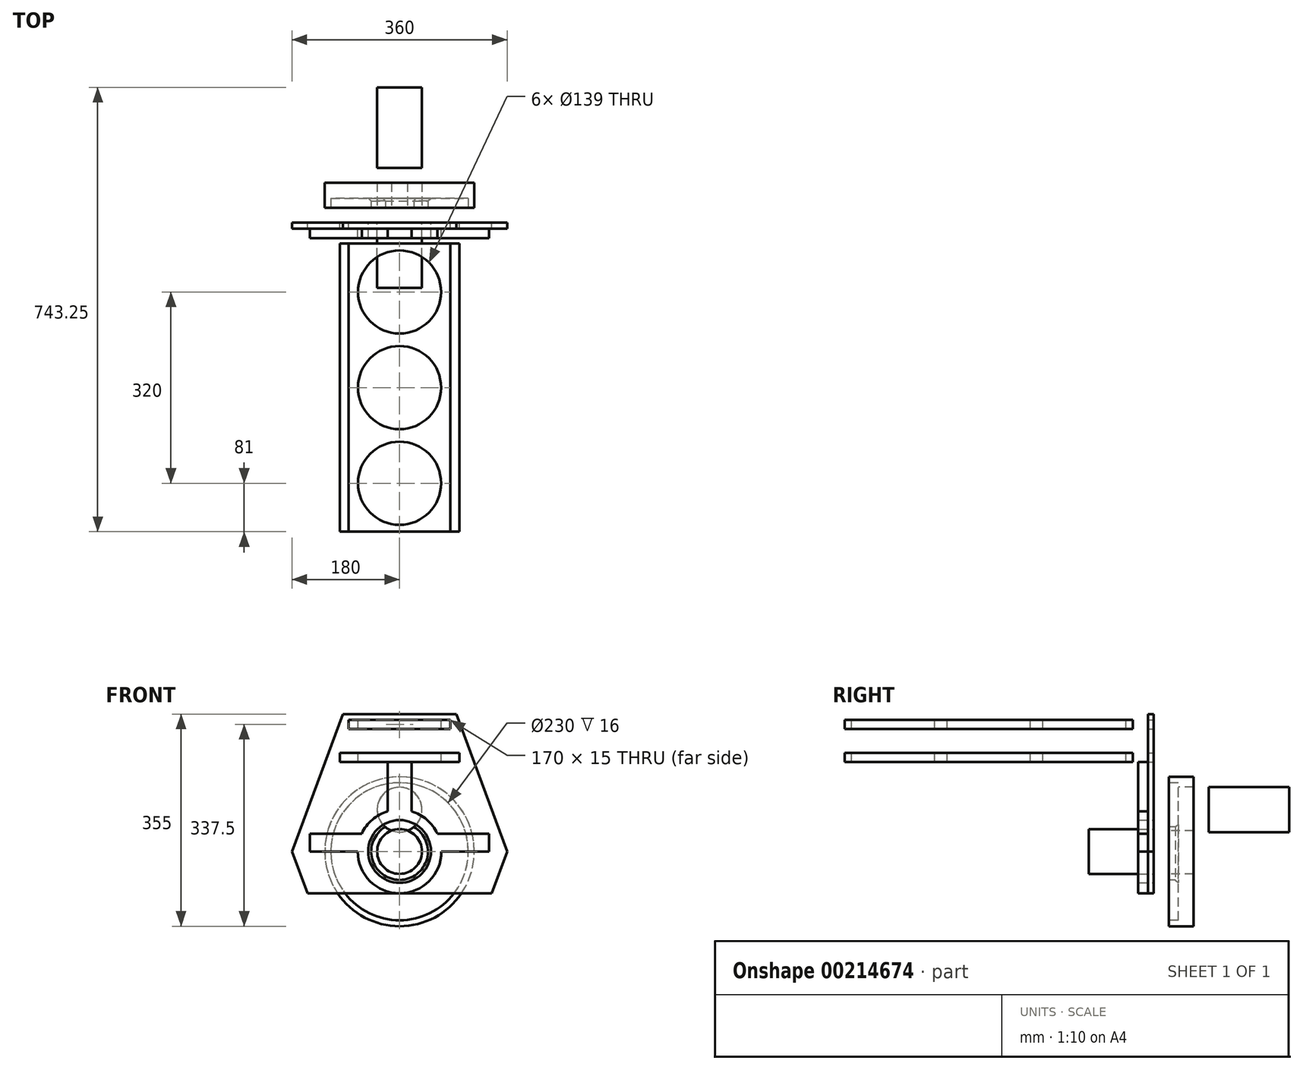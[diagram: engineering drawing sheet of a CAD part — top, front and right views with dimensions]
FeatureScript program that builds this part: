
annotation { "Feature Type Name" : "Feature", "Feature Type Description" : "" }
export const myFeature = defineFeature(function(context is Context, id is Id, definition is map)
    precondition{}
    {
        {
            var Q0;
            Q0=qCreatedBy(makeId("Front.planeOp"),FACE);
            var sketch = newSketch(context, id + "F0", { "sketchPlane" : qUnion([Q0])});
            skCircle(sketch, "E0", {"center": v(0, 0) * mm, "radius": 70 * mm});
            skCircle(sketch, "E1", {"center": v(0, 0) * mm, "radius": 125 * mm});
            skLineSegment(sketch, "E2", {"start": v(0, 0) * mm, "end": v(0, 70) * mm});
            skCircle(sketch, "E3", {"center": v(0, 70) * mm, "radius": 37.5 * mm});
            skCircle(sketch, "E4", {"center": v(0, 0) * mm, "radius": 37.5 * mm});
            skSolve(sketch);
        }
        {
            var Q0;
            Q0=makeQuery(id+"F0.imprint","IMPRINT",FACE,{"disambiguationData":[TD([[makeQuery(id+"F0.imprint","IMPRINT",EDGE,{"derivedFrom":sQuery(id+"F0.wireOp",EDGE,"E1")}),1.0]])]});
            var Q1;
            {var subQ0=sQuery(id+"F0.wireOp",EDGE,"E3");var subQ1=sQuery(id+"F0.wireOp",EDGE,"E0");var subQ2=makeQuery(id+"F0.imprint","INTERSECT",VERTEX,{"disambiguationData":[OD(0.0)],"derivedFrom":[subQ1,subQ0]});Q1=makeQuery(id+"F0.imprint","IMPRINT",FACE,{"disambiguationData":[TD([[makeQuery(id+"F0.imprint","IMPRINT",EDGE,{"disambiguationData":[TD([[subQ2,1.0]])],"derivedFrom":subQ1}),1.0]])]});}
            extrude(context, id + "F1", {"entities" : qUnion([Q0, Q1]), "oppositeDirection" : true, "depth" : 41.75 * mm});
        }
        {
            var Q0;
            Q0=makeQuery(id+"F1.opExtrude","CAP_FACE",FACE,{"disambiguationData":[OSD([sQuery(id+"F0.wireOp",EDGE,"E1"),sQuery(id+"F0.wireOp",EDGE,"E3"),sQuery(id+"F0.wireOp",EDGE,"E4")])],"isStart":true});
            cPlane(context, id + "F2", {"entities" : qUnion([Q0]), "cplaneType" : CPlaneType.OFFSET, "offset" : 25 * mm, "width" : 150 * mm, "height" : 150 * mm});
        }
        {
            var Q0;
            Q0=qCreatedBy(id+"F2.planeOp",FACE);
            var sketch = newSketch(context, id + "F3", { "sketchPlane" : qUnion([Q0])});
            skCircle(sketch, "E5", {"center": v(0, 0) * mm, "radius": 37.5 * mm});
            skSolve(sketch);
        }
        {
            var Q0;
            Q0=makeQuery(id+"F3.imprint","IMPRINT",FACE,{"disambiguationData":[TD([[makeQuery(id+"F3.imprint","IMPRINT",EDGE,{"derivedFrom":sQuery(id+"F3.wireOp",EDGE,"E5")}),1.0]])]});
            extrude(context, id + "F4", {"entities" : qUnion([Q0]), "depth" : 109 * mm});
        }
        {
            var Q0;
            Q0=makeQuery(id+"F1.opExtrude","CAP_FACE",FACE,{"disambiguationData":[OSD([sQuery(id+"F0.wireOp",EDGE,"E1"),sQuery(id+"F0.wireOp",EDGE,"E3"),sQuery(id+"F0.wireOp",EDGE,"E4")])],"isStart":false});
            cPlane(context, id + "F5", {"entities" : qUnion([Q0]), "cplaneType" : CPlaneType.OFFSET, "offset" : 25 * mm, "width" : 150 * mm, "height" : 150 * mm});
        }
        {
            var Q0;
            Q0=qCreatedBy(id+"F5.planeOp",FACE);
            var sketch = newSketch(context, id + "F6", { "sketchPlane" : qUnion([Q0])});
            skCircle(sketch, "E6", {"center": v(0, 70) * mm, "radius": 37.5 * mm});
            skSolve(sketch);
        }
        {
            var Q0;
            Q0=makeQuery(id+"F6.imprint","IMPRINT",FACE,{"disambiguationData":[TD([[makeQuery(id+"F6.imprint","IMPRINT",EDGE,{"derivedFrom":sQuery(id+"F6.wireOp",EDGE,"E6")}),1.0]])]});
            extrude(context, id + "F7", {"entities" : qUnion([Q0]), "depth" : 134.5 * mm});
        }
        {
            var Q0;
            Q0=qCreatedBy(id+"F2.planeOp",FACE);
            var sketch = newSketch(context, id + "F8", { "sketchPlane" : qUnion([Q0])});
            skLineSegment(sketch, "E7", {"start": v(0, 0) * mm, "end": v(180, 0) * mm});
            skLineSegment(sketch, "E8", {"start": v(100, 150) * mm, "end": v(0, 150) * mm});
            skLineSegment(sketch, "E9", {"start": v(95, 230) * mm, "end": v(0, 230) * mm});
            skLineSegment(sketch, "E10", {"start": v(180, 0) * mm, "end": v(95, 230) * mm});
            skLineSegment(sketch, "E11.MirrorCS", {"start": v(180, 0) * mm, "end": v(154.13, -70) * mm});
            skLineSegment(sketch, "E12", {"start": v(154.13, -70) * mm, "end": v(0, -70) * mm});
            skPoint(sketch, "E13.orphan", {"position": v(95, -230) * mm});
            skLineSegment(sketch, "E14", {"start": v(0, 0) * mm, "end": v(0, -98.28) * mm});
            skLineSegment(sketch, "E15.MirrorCS", {"start": v(-95, 230) * mm, "end": v(0, 230) * mm});
            skLineSegment(sketch, "E16.MirrorCS", {"start": v(-180, 0) * mm, "end": v(-95, 230) * mm});
            skLineSegment(sketch, "E17.MirrorCS", {"start": v(-180, 0) * mm, "end": v(-154.13, -70) * mm});
            skLineSegment(sketch, "E18.MirrorCS", {"start": v(-154.13, -70) * mm, "end": v(0, -70) * mm});
            skCircle(sketch, "E19", {"center": v(0, 0) * mm, "radius": 52.5 * mm});
            skLineSegment(sketch, "E20", {"start": v(0, 230) * mm, "end": v(0, 205) * mm});
            skLineSegment(sketch, "E21", {"start": v(0, 205) * mm, "end": v(85, 205) * mm});
            skLineSegment(sketch, "E22", {"start": v(85, 205) * mm, "end": v(85, 220) * mm});
            skLineSegment(sketch, "E23", {"start": v(85, 220) * mm, "end": v(0, 220) * mm});
            skLineSegment(sketch, "E24", {"start": v(0, 150) * mm, "end": v(0, 205) * mm});
            skLineSegment(sketch, "E25", {"start": v(0, 165) * mm, "end": v(100, 165) * mm});
            skLineSegment(sketch, "E26", {"start": v(100, 165) * mm, "end": v(100, 150) * mm});
            skLineSegment(sketch, "E27.MirrorCS", {"start": v(0, 205) * mm, "end": v(-85, 205) * mm});
            skLineSegment(sketch, "E28.MirrorCS", {"start": v(-85, 220) * mm, "end": v(0, 220) * mm});
            skLineSegment(sketch, "E29.MirrorCS", {"start": v(-85, 205) * mm, "end": v(-85, 220) * mm});
            skLineSegment(sketch, "E30.MirrorCS", {"start": v(0, 165) * mm, "end": v(-100, 165) * mm});
            skLineSegment(sketch, "E31.MirrorCS", {"start": v(-100, 150) * mm, "end": v(0, 150) * mm});
            skLineSegment(sketch, "E32.MirrorCS", {"start": v(-100, 165) * mm, "end": v(-100, 150) * mm});
            skSolve(sketch);
        }
        {
            var Q0;
            Q0=makeQuery(id+"F8.imprint","IMPRINT",FACE,{"disambiguationData":[TD([[makeQuery(id+"F8.imprint","IMPRINT",EDGE,{"derivedFrom":sQuery(id+"F8.wireOp",EDGE,"E9")}),1.0]])]});
            var Q1;
            {var subQ4=sQuery(id+"F8.wireOp",EDGE,"E11.MirrorCS");Q1=makeQuery(id+"F8.imprint","IMPRINT",FACE,{"disambiguationData":[TD([[makeQuery(id+"F8.imprint","IMPRINT",EDGE,{"derivedFrom":subQ4}),-1.0]])]});}
            extrude(context, id + "F9", {"entities" : qUnion([Q0, Q1]), "depth" : 10 * mm});
        }
        {
            var Q0;
            Q0=makeQuery(id+"F9.opExtrude","CAP_FACE",FACE,{"disambiguationData":[OSD([sQuery(id+"F8.wireOp",EDGE,"E8"),sQuery(id+"F8.wireOp",EDGE,"E9"),sQuery(id+"F8.wireOp",EDGE,"E10"),sQuery(id+"F8.wireOp",EDGE,"E11.MirrorCS"),sQuery(id+"F8.wireOp",EDGE,"E12"),sQuery(id+"F8.wireOp",EDGE,"E15.MirrorCS"),sQuery(id+"F8.wireOp",EDGE,"E16.MirrorCS"),sQuery(id+"F8.wireOp",EDGE,"E17.MirrorCS"),sQuery(id+"F8.wireOp",EDGE,"E18.MirrorCS"),sQuery(id+"F8.wireOp",EDGE,"E19"),sQuery(id+"F8.wireOp",EDGE,"E21"),sQuery(id+"F8.wireOp",EDGE,"E22"),sQuery(id+"F8.wireOp",EDGE,"E23"),sQuery(id+"F8.wireOp",EDGE,"E25"),sQuery(id+"F8.wireOp",EDGE,"E26"),sQuery(id+"F8.wireOp",EDGE,"E27.MirrorCS"),sQuery(id+"F8.wireOp",EDGE,"E28.MirrorCS"),sQuery(id+"F8.wireOp",EDGE,"E29.MirrorCS"),sQuery(id+"F8.wireOp",EDGE,"E30.MirrorCS"),sQuery(id+"F8.wireOp",EDGE,"E31.MirrorCS"),sQuery(id+"F8.wireOp",EDGE,"E32.MirrorCS")])],"isStart":false});
            var sketch = newSketch(context, id + "F10", { "sketchPlane" : qUnion([Q0])});
            skCircle(sketch, "E33", {"center": v(0, 0) * mm, "radius": 70 * mm});
            skLineSegment(sketch, "E34", {"start": v(0, 70) * mm, "end": v(0, 150) * mm});
            skLineSegment(sketch, "E35.0", {"start": v(20, 67.08) * mm, "end": v(20, 150) * mm});
            skLineSegment(sketch, "E36", {"start": v(70, 0) * mm, "end": v(150, 0) * mm});
            skLineSegment(sketch, "E37.0", {"start": v(63.25, 30) * mm, "end": v(150, 30) * mm});
            skLineSegment(sketch, "E38", {"start": v(150, 0) * mm, "end": v(150, 30) * mm});
            skLineSegment(sketch, "E39.MirrorCS", {"start": v(-20, 67.08) * mm, "end": v(-20, 150) * mm});
            skLineSegment(sketch, "E40.MirrorCS", {"start": v(-63.25, 30) * mm, "end": v(-150, 30) * mm});
            skLineSegment(sketch, "E41.MirrorCS", {"start": v(-70, 0) * mm, "end": v(-150, 0) * mm});
            skLineSegment(sketch, "E42.MirrorCS", {"start": v(-150, 0) * mm, "end": v(-150, 30) * mm});
            skCircle(sketch, "E43", {"center": v(0, 0) * mm, "radius": 52.5 * mm});
            skLineSegment(sketch, "E44", {"start": v(-20, 150) * mm, "end": v(20, 150) * mm});
            skSolve(sketch);
        }
        {
            var Q0;
            {var subQ0=sQuery(id+"F10.wireOp",EDGE,"E34");Q0=makeQuery(id+"F10.imprint","IMPRINT",FACE,{"disambiguationData":[TD([[makeQuery(id+"F10.imprint","IMPRINT",EDGE,{"derivedFrom":subQ0}),1.0]])]});}
            var Q1;
            {var subQ0=sQuery(id+"F10.wireOp",EDGE,"E34");Q1=makeQuery(id+"F10.imprint","IMPRINT",FACE,{"disambiguationData":[TD([[makeQuery(id+"F10.imprint","IMPRINT",EDGE,{"derivedFrom":subQ0}),-1.0]])]});}
            var Q2;
            Q2=makeQuery(id+"F10.imprint","IMPRINT",FACE,{"disambiguationData":[TD([[makeQuery(id+"F10.imprint","IMPRINT",EDGE,{"derivedFrom":sQuery(id+"F10.wireOp",EDGE,"E43")}),-1.0]])]});
            var Q3;
            {var subQ0=sQuery(id+"F10.wireOp",EDGE,"E36");Q3=makeQuery(id+"F10.imprint","IMPRINT",FACE,{"disambiguationData":[TD([[makeQuery(id+"F10.imprint","IMPRINT",EDGE,{"derivedFrom":subQ0}),1.0]])]});}
            var Q4;
            {var subQ0=sQuery(id+"F10.wireOp",EDGE,"E40.MirrorCS");Q4=makeQuery(id+"F10.imprint","IMPRINT",FACE,{"disambiguationData":[TD([[makeQuery(id+"F10.imprint","IMPRINT",EDGE,{"derivedFrom":subQ0}),1.0]])]});}
            extrude(context, id + "F11", {"entities" : qUnion([Q0, Q1, Q2, Q3, Q4]), "operationType" : NewBodyOperationType.ADD, "depth" : 16 * mm});
        }
        {
            var Q0;
            Q0=makeQuery(id+"F9.opExtrude","CAP_FACE",FACE,{"disambiguationData":[OSD([sQuery(id+"F8.wireOp",EDGE,"E8"),sQuery(id+"F8.wireOp",EDGE,"E9"),sQuery(id+"F8.wireOp",EDGE,"E10"),sQuery(id+"F8.wireOp",EDGE,"E11.MirrorCS"),sQuery(id+"F8.wireOp",EDGE,"E12"),sQuery(id+"F8.wireOp",EDGE,"E15.MirrorCS"),sQuery(id+"F8.wireOp",EDGE,"E16.MirrorCS"),sQuery(id+"F8.wireOp",EDGE,"E17.MirrorCS"),sQuery(id+"F8.wireOp",EDGE,"E18.MirrorCS"),sQuery(id+"F8.wireOp",EDGE,"E19"),sQuery(id+"F8.wireOp",EDGE,"E21"),sQuery(id+"F8.wireOp",EDGE,"E22"),sQuery(id+"F8.wireOp",EDGE,"E23"),sQuery(id+"F8.wireOp",EDGE,"E25"),sQuery(id+"F8.wireOp",EDGE,"E26"),sQuery(id+"F8.wireOp",EDGE,"E27.MirrorCS"),sQuery(id+"F8.wireOp",EDGE,"E28.MirrorCS"),sQuery(id+"F8.wireOp",EDGE,"E29.MirrorCS"),sQuery(id+"F8.wireOp",EDGE,"E30.MirrorCS"),sQuery(id+"F8.wireOp",EDGE,"E31.MirrorCS"),sQuery(id+"F8.wireOp",EDGE,"E32.MirrorCS")])],"isStart":false});
            cPlane(context, id + "F12", {"entities" : qUnion([Q0]), "cplaneType" : CPlaneType.OFFSET, "offset" : 25 * mm, "width" : 150 * mm, "height" : 150 * mm});
        }
        {
            var Q0;
            Q0=qCreatedBy(id+"F12.planeOp",FACE);
            var sketch = newSketch(context, id + "F13", { "sketchPlane" : qUnion([Q0])});
            skLineSegment(sketch, "E45.bottom", {"start": v(-85, 220) * mm, "end": v(85, 220) * mm});
            skLineSegment(sketch, "E45.top", {"start": v(-85, 205) * mm, "end": v(85, 205) * mm});
            skLineSegment(sketch, "E45.left", {"start": v(-85, 220) * mm, "end": v(-85, 205) * mm});
            skLineSegment(sketch, "E45.right", {"start": v(85, 220) * mm, "end": v(85, 205) * mm});
            skLineSegment(sketch, "E46.bottom", {"start": v(-100, 165) * mm, "end": v(100, 165) * mm});
            skLineSegment(sketch, "E46.top", {"start": v(-100, 150) * mm, "end": v(100, 150) * mm});
            skLineSegment(sketch, "E46.left", {"start": v(-100, 165) * mm, "end": v(-100, 150) * mm});
            skLineSegment(sketch, "E46.right", {"start": v(100, 165) * mm, "end": v(100, 150) * mm});
            skSolve(sketch);
        }
        {
            var Q0;
            Q0=makeQuery(id+"F13.imprint","IMPRINT",FACE,{"disambiguationData":[TD([[makeQuery(id+"F13.imprint","IMPRINT",EDGE,{"derivedFrom":sQuery(id+"F13.wireOp",EDGE,"E45.bottom")}),-1.0]])]});
            var Q1;
            Q1=makeQuery(id+"F13.imprint","IMPRINT",FACE,{"disambiguationData":[TD([[makeQuery(id+"F13.imprint","IMPRINT",EDGE,{"derivedFrom":sQuery(id+"F13.wireOp",EDGE,"E46.bottom")}),-1.0]])]});
            extrude(context, id + "F14", {"entities" : qUnion([Q0, Q1]), "depth" : 482 * mm});
        }
        {
            var Q0;
            Q0=makeQuery(id+"F14.opExtrude","SWEPT_FACE",FACE,{"disambiguationData":[OSD([sQuery(id+"F13.wireOp",EDGE,"E45.bottom")])]});
            var sketch = newSketch(context, id + "F15", { "sketchPlane" : qUnion([Q0])});
            skCircle(sketch, "E47", {"center": v(0, -461) * mm, "radius": 69.5 * mm});
            skPoint(sketch, "E47.centerSnap0", {"position": v(0, -542) * mm});
            skCircle(sketch, "E48", {"center": v(0, -301) * mm, "radius": 69.5 * mm});
            skCircle(sketch, "E49", {"center": v(0, -141) * mm, "radius": 69.5 * mm});
            skSolve(sketch);
        }
        {
            var Q0;
            Q0=makeQuery(id+"F15.imprint","IMPRINT",FACE,{"disambiguationData":[TD([[makeQuery(id+"F15.imprint","IMPRINT",EDGE,{"derivedFrom":sQuery(id+"F15.wireOp",EDGE,"E47")}),1.0]])]});
            var Q1;
            Q1=makeQuery(id+"F15.imprint","IMPRINT",FACE,{"disambiguationData":[TD([[makeQuery(id+"F15.imprint","IMPRINT",EDGE,{"derivedFrom":sQuery(id+"F15.wireOp",EDGE,"E48")}),1.0]])]});
            var Q2;
            Q2=makeQuery(id+"F15.imprint","IMPRINT",FACE,{"disambiguationData":[TD([[makeQuery(id+"F15.imprint","IMPRINT",EDGE,{"derivedFrom":sQuery(id+"F15.wireOp",EDGE,"E49")}),1.0]])]});
            extrude(context, id + "F16", {"entities" : qUnion([Q0, Q1, Q2]), "operationType" : NewBodyOperationType.REMOVE, "oppositeDirection" : true, "depth" : 100 * mm});
        }
        {
            var Q0;
            Q0=makeQuery(id+"F0.imprint","IMPRINT",FACE,{"disambiguationData":[TD([[makeQuery(id+"F0.imprint","IMPRINT",EDGE,{"derivedFrom":sQuery(id+"F0.wireOp",EDGE,"E1")}),1.0]])]});
            var sketch = newSketch(context, id + "F17", { "sketchPlane" : qUnion([Q0])});
            skCircle(sketch, "E50", {"center": v(0, 0) * mm, "radius": 115 * mm});
            skCircle(sketch, "E51", {"center": v(0, 0) * mm, "radius": 47.5 * mm});
            skSolve(sketch);
        }
        {
            var Q0;
            Q0=makeQuery(id+"F17.imprint","IMPRINT",FACE,{"disambiguationData":[TD([[makeQuery(id+"F17.imprint","IMPRINT",EDGE,{"derivedFrom":sQuery(id+"F17.wireOp",EDGE,"E50")}),1.0]])]});
            var Q1;
            Q1=makeQuery(id+"F17.imprint","IMPRINT",FACE,{"disambiguationData":[TD([[makeQuery(id+"F17.imprint","IMPRINT",EDGE,{"derivedFrom":sQuery(id+"F17.wireOp",EDGE,"E51")}),-1.0]])]});
            extrude(context, id + "F18", {"entities" : qUnion([Q0, Q1]), "operationType" : NewBodyOperationType.REMOVE, "oppositeDirection" : true, "depth" : 16 * mm});
        }
        {
            var Q0;
            Q0=makeQuery(id+"F18.boolean.opBoolean","COPY",EDGE,{"derivedFrom":makeQuery(id+"F18.opExtrude","CAP_EDGE",EDGE,{"disambiguationData":[OSD([sQuery(id+"F17.wireOp",EDGE,"E51")])],"isStart":false})});
            chamfer(context, id + "F19", {"entities" : qUnion([Q0]), "width" : 5 * mm, "tangentPropagation" : true});
        }
    });
